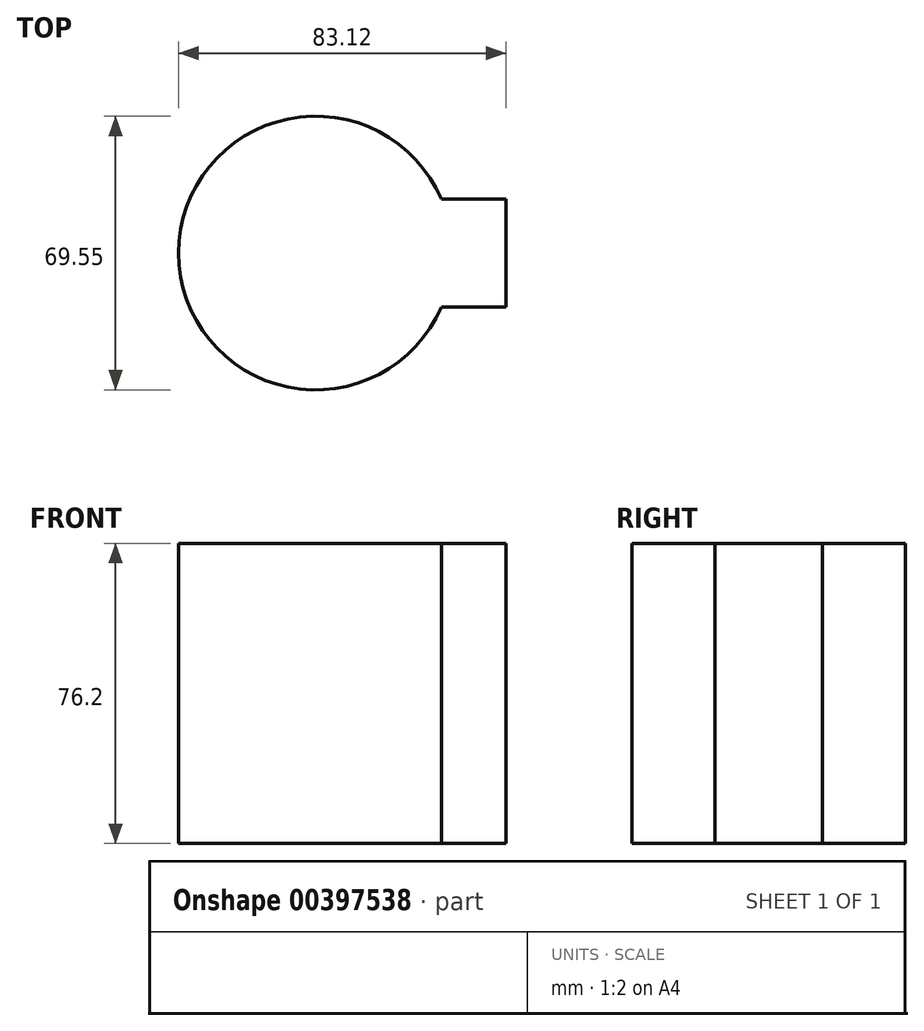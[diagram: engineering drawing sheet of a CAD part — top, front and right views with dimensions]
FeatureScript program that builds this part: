
annotation { "Feature Type Name" : "Feature", "Feature Type Description" : "" }
export const myFeature = defineFeature(function(context is Context, id is Id, definition is map)
    precondition{}
    {
        {
            var Q0;
            Q0=qCreatedBy(makeId("Top.planeOp"),FACE);
            var sketch = newSketch(context, id + "F0", { "sketchPlane" : qUnion([Q0])});
            skLineSegment(sketch, "E0.bottom", {"start": v(0, 0) * mm, "end": v(48.34, 0) * mm});
            skLineSegment(sketch, "E0.top", {"start": v(0, -27.39) * mm, "end": v(48.34, -27.39) * mm});
            skLineSegment(sketch, "E0.left", {"start": v(0, 0) * mm, "end": v(0, -27.39) * mm});
            skLineSegment(sketch, "E0.right", {"start": v(48.34, 0) * mm, "end": v(48.34, -27.39) * mm});
            skCircle(sketch, "E1", {"center": v(0, -13.7) * mm, "radius": 34.78 * mm});
            skSolve(sketch);
        }
        {
            var Q0;
            Q0 = qSketchRegion(id + "F0", true);
            extrude(context, id + "F1", {"entities" : qUnion([Q0]), "depth" : 76.2 * mm});
        }
        {
            var Q0;
            Q0=makeQuery(id+"F1.opExtrude","CAP_FACE",FACE,{"disambiguationData":[OSD([sQuery(id+"F0.wireOp",EDGE,"E0.bottom"),sQuery(id+"F0.wireOp",EDGE,"E0.top"),sQuery(id+"F0.wireOp",EDGE,"E0.right"),sQuery(id+"F0.wireOp",EDGE,"E1")])],"isStart":false});
            var sketch = newSketch(context, id + "F2", { "sketchPlane" : qUnion([Q0])});
            skLineSegment(sketch, "E2.0", {"start": v(38.94, -9.4) * mm, "end": v(25.01, -9.4) * mm});
            skLineSegment(sketch, "E2.1", {"start": v(38.94, -17.99) * mm, "end": v(38.94, -9.4) * mm});
            skLineSegment(sketch, "E2.2", {"start": v(25.01, -17.99) * mm, "end": v(38.94, -17.99) * mm});
            skArc(sketch, "E2.3", {"start": v(25.01, -9.4) * mm, "mid": v(-25.38, -13.7) * mm, "end": v(25.01, -17.99) * mm});
            skSolve(sketch);
        }
        {
            var Q0;
            Q0=makeQuery(id+"F2.imprint","IMPRINT",FACE,{"disambiguationData":[TD([[makeQuery(id+"F2.imprint","IMPRINT",EDGE,{"derivedFrom":sQuery(id+"F2.wireOp",EDGE,"E2.0")}),1.0]])]});
            extrude(context, id + "F3", {"entities" : qUnion([Q0]), "operationType" : NewBodyOperationType.ADD, "depth" : -25.4 * mm});
        }
    });
